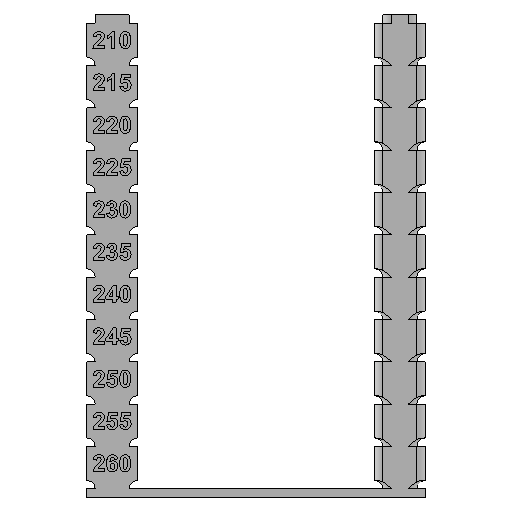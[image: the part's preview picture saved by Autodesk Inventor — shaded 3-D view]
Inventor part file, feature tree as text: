
AUTODESK INVENTOR PART (.ipt)
format: ipt  version: 2025.3 (Build 293356000, 356)  size: 1,708,032 bytes
history: native  units: mm
features: other x8, extrude x4, sketch x2, mirror x2, fillet x2, pattern_linear x2
ambient origin geometry x8: Origin, YZ Plane, XZ Plane, XY Plane, X Axis, Y Axis, Z Axis, Center Point
bodies: Body1 (feature_tree)
feature tree (20):
  other  "實體1"
  other  "temp_tower"
  sketch  "草圖1"
  extrude  "擠出1"  Depth=40.0mm
  extrude  "擠出2"  Depth=5.0mm
  mirror  "鏡射1"
  extrude  "擠出3"  Depth=6.0mm
  extrude  "擠出4"  Depth=1.0mm
  mirror  "鏡射2"
  fillet  "圓角1"  Radius=1.0mm
  pattern_linear  "矩形陣列1"  Spacing1=4.0mm  [1 undecoded]
  other  "合併1"
  fillet  "圓角2"  Radius=1.0mm
  pattern_linear  "矩形陣列2"  Spacing1=1.0mm  [1 undecoded]
  other  "浮雕1"
  other  "實體2"
  other  "陣列 實體2:1"
  other  "實體3"
  sketch  "草圖2"
  other  "MeshFeature1"
note: 2 required parameter values undecoded (feature->parameter linkage not recoverable at this tier; creation-order binding heuristic only, values carry confidence <= 0.55)
